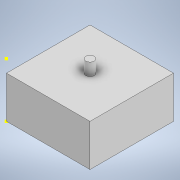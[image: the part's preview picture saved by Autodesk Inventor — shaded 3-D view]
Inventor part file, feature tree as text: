
AUTODESK INVENTOR PART (.ipt)
format: ipt  version: 2021 (Build 250183000, 183)  size: 94,720 bytes
history: native  units: in
note: dims shown in document units (in); Inventor stores cm internally (conversion verified against a paired STEP export)
features: sketch x4, extrude x2
ambient origin geometry x8: Origin, YZ Plane, XZ Plane, XY Plane, X Axis, Y Axis, Z Axis, Center Point
bodies: Solid1 (feature_tree)
feature tree (6):
  sketch  "Sketch1"  dims[d0=3.937in d1=3.937in]
  extrude  "Extrusion1"  Depth=3.937in
  extrude  "Extrusion2"  Depth=0.3937in
  sketch  "Sketch4"
  sketch  "Sketch2"  dims[d2=1.9685in d3=0.0in d4=0.3937in]
  sketch  "Sketch3"  dims[d5=0.5906in d6=0.0in]
